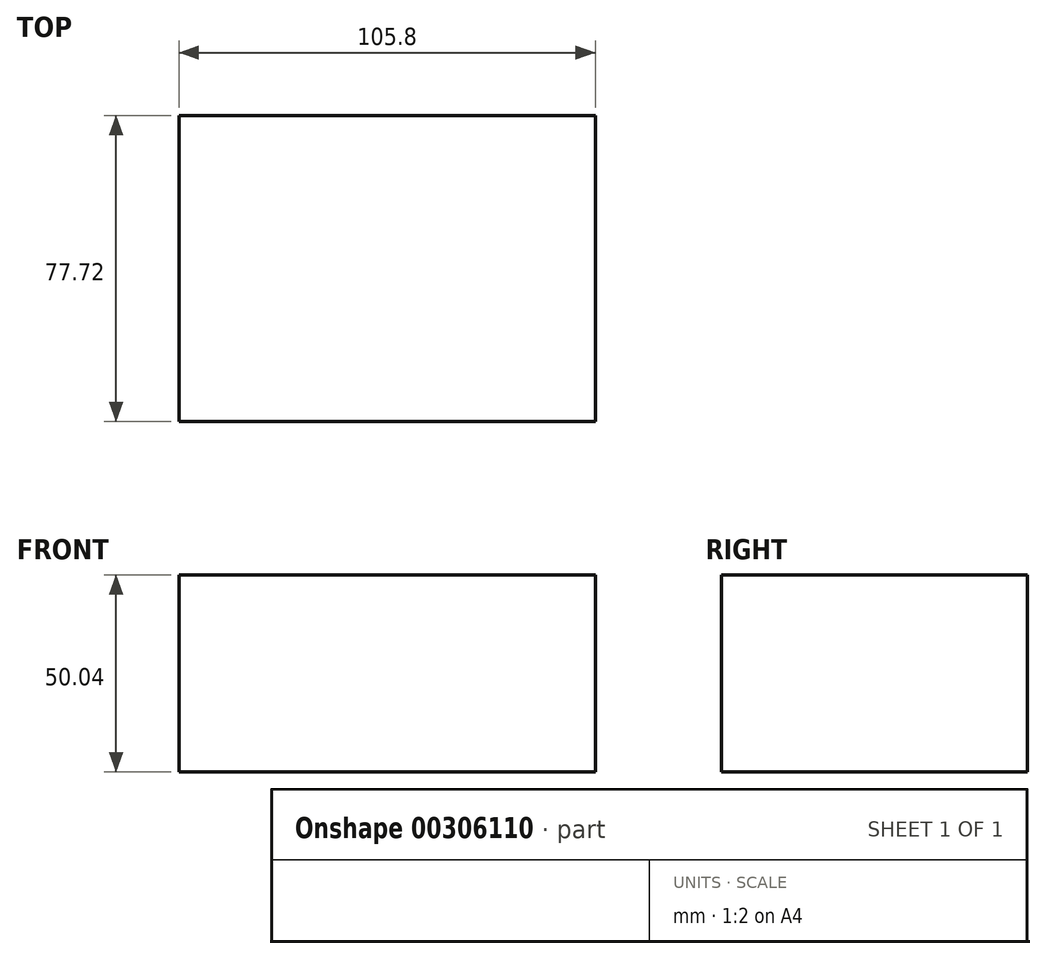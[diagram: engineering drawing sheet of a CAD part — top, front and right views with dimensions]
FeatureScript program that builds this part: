
annotation { "Feature Type Name" : "Feature", "Feature Type Description" : "" }
export const myFeature = defineFeature(function(context is Context, id is Id, definition is map)
    precondition{}
    {
        {
            var Q0;
            Q0=qCreatedBy(makeId("Front.planeOp"),FACE);
            var sketch = newSketch(context, id + "F0", { "sketchPlane" : qUnion([Q0])});
            skLineSegment(sketch, "E0.bottom", {"start": v(-44, 9.64) * mm, "end": v(61.81, 9.64) * mm});
            skLineSegment(sketch, "E0.top", {"start": v(-44, -40.4) * mm, "end": v(61.81, -40.4) * mm});
            skLineSegment(sketch, "E0.left", {"start": v(-44, 9.64) * mm, "end": v(-44, -40.4) * mm});
            skLineSegment(sketch, "E0.right", {"start": v(61.81, 9.64) * mm, "end": v(61.81, -40.4) * mm});
            skSolve(sketch);
        }
        {
            var Q0;
            Q0=makeQuery(id+"F0.imprint","IMPRINT",FACE,{"disambiguationData":[TD([[makeQuery(id+"F0.imprint","IMPRINT",EDGE,{"derivedFrom":sQuery(id+"F0.wireOp",EDGE,"E0.bottom")}),-1.0]])]});
            extrude(context, id + "F1", {"entities" : qUnion([Q0]), "depth" : 77.72 * mm, "offsetDistance" : 25.4 * mm});
        }
    });
